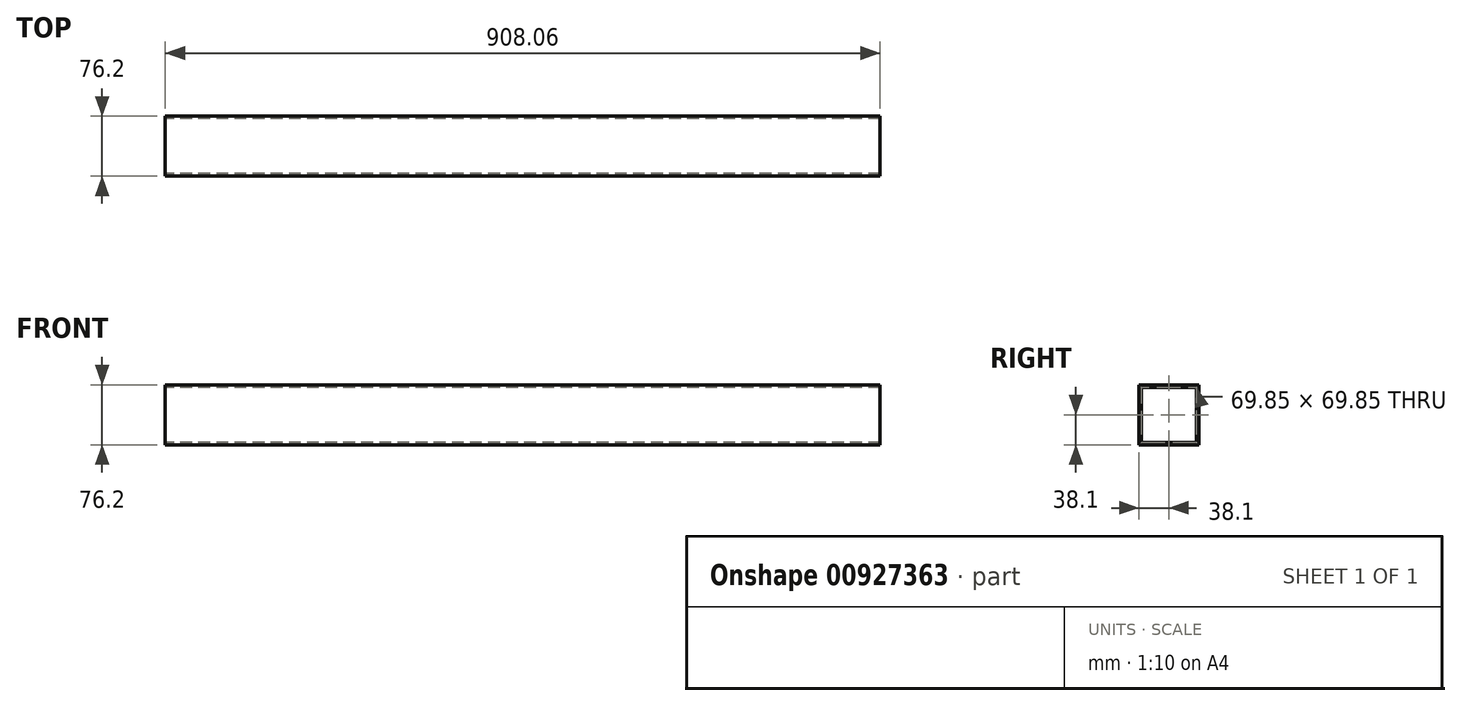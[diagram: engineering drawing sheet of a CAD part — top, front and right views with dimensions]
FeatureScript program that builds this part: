
annotation { "Feature Type Name" : "Feature", "Feature Type Description" : "" }
export const myFeature = defineFeature(function(context is Context, id is Id, definition is map)
    precondition{}
    {
        {
            var Q0;
            Q0=qCreatedBy(makeId("Right.planeOp"),FACE);
            var sketch = newSketch(context, id + "F0", { "sketchPlane" : qUnion([Q0])});
            skLineSegment(sketch, "E0.bottom", {"start": v(-38.1, 38.1) * mm, "end": v(38.1, 38.1) * mm});
            skLineSegment(sketch, "E0.top", {"start": v(-38.1, -38.1) * mm, "end": v(38.1, -38.1) * mm});
            skLineSegment(sketch, "E0.left", {"start": v(-38.1, 38.1) * mm, "end": v(-38.1, -38.1) * mm});
            skLineSegment(sketch, "E0.right", {"start": v(38.1, 38.1) * mm, "end": v(38.1, -38.1) * mm});
            skLineSegment(sketch, "E1.bottom", {"start": v(34.93, 34.92) * mm, "end": v(-34.93, 34.92) * mm});
            skLineSegment(sketch, "E1.top", {"start": v(34.93, -34.92) * mm, "end": v(-34.93, -34.92) * mm});
            skLineSegment(sketch, "E1.left", {"start": v(34.92, 34.92) * mm, "end": v(34.93, -34.93) * mm});
            skLineSegment(sketch, "E1.right", {"start": v(-34.93, 34.92) * mm, "end": v(-34.92, -34.93) * mm});
            skPoint(sketch, "E1.middle", {"position": v(0, 0) * mm});
            skSolve(sketch);
        }
        {
            var Q0;
            Q0=makeQuery(id+"F0.imprint","IMPRINT",FACE,{"disambiguationData":[TD([[makeQuery(id+"F0.imprint","IMPRINT",EDGE,{"derivedFrom":sQuery(id+"F0.wireOp",EDGE,"E0.bottom")}),-1.0]])]});
            extrude(context, id + "F1", {"entities" : qUnion([Q0]), "depth" : 454.02 * mm, "offsetDistance" : 25.4 * mm, "hasSecondDirection" : true, "secondDirectionOppositeDirection" : true, "secondDirectionDepth" : 454.02 * mm});
        }
    });
